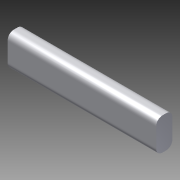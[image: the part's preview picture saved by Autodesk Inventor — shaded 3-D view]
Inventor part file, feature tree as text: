
AUTODESK INVENTOR PART (.ipt)
format: ipt  version: 2012 (Build 160160000, 160)  size: 91,136 bytes
history: native  units: mm
features: extrude x1, sketch x1
ambient origin geometry x8: Origin, YZ Plane, XZ Plane, XY Plane, X Axis, Y Axis, Z Axis, Center Point
bodies: Solid1 (feature_tree)
feature tree (2):
  extrude  "Extrusion1"  Depth=23.0mm
  sketch  "Sketch1"  dims[d0=212.0mm d1=23.0mm d2=46.0mm d3=0.0mm d5=10.0mm]
